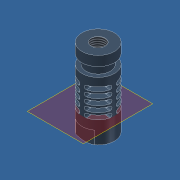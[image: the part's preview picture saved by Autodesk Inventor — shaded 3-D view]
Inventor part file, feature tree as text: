
AUTODESK INVENTOR PART (.ipt)
format: ipt  version: unknown  size: 470,016 bytes
history: native  units: mm
features: sketch x7, hole x3, extrude x3, pattern_circular x2, pattern_linear x2, revolve x1, plane x1, fillet x1, projected_geometry x1
ambient origin geometry x8: Origin, YZ Plane, XZ Plane, XY Plane, X Axis, Y Axis, Z Axis, Center Point
feature tree (21):
  revolve  "Revolution1"  [1 undecoded]
  hole  "Hole1"  [1 undecoded]
  hole  "Hole2"  [1 undecoded]
  plane  "Work Plane1"
  extrude  "Extrusion1"  Depth=4.8mm
  fillet  "Fillet2"  [1 undecoded]
  pattern_circular  "Circular Pattern1"  [2 undecoded]
  pattern_linear  "Rectangular Pattern1"  Spacing1=1.368338mm  [1 undecoded]
  extrude  "Extrusion2"  Depth=12.971287mm
  extrude  "Extrusion3"  Depth=2.0mm TaperAngle=0.0deg
  pattern_linear  "Rectangular Pattern2"  Spacing1=1.0mm  [1 undecoded]
  pattern_circular  "Circular Pattern2"  Count=4 Angle=360.0deg
  hole  "Hole4"  [1 undecoded]
  sketch  "Sketch2"  dims[d0=3.25mm d1=6.0mm]
  sketch  "Sketch3"  dims[d2=40.0mm d3=4.6mm]
  sketch  "Sketch4"  dims[d4=8.0mm d5=60.0deg]
  sketch  "Sketch5"  dims[d6=5.0mm d7=4.8mm d8=90.0deg]
  sketch  "Sketch6"  dims[d9=6.917mm d10=11.5mm d11=4.0mm d12=2.0mm d13=90.0deg d14=11.5mm d15=20.594885mm]
  sketch  "Sketch8"  dims[d16=6.917mm d17=7.6mm d18=4.0mm d19=2.0mm d20=90.0deg d21=7.5mm d22=20.594885mm]
  sketch  "Sketch9"  dims[d23=-12.5mm d24=3.8mm d26=1.368338mm d27=12.971287mm d28=2.0mm d29=0.0mm d31=1.0mm d33=40.0mm d34=360.0deg d36=50.0mm d38=3.0mm d39=8.0mm d40=13.0mm d41=6.5mm d42=8.0mm d43=2.0mm d44=0.0mm d55=2.0mm d56=2.8mm d57=2.0mm d58=0.0mm d59=40.0mm d61=3.0mm d62=40.0mm d63=360.0deg d65=8.0mm d66=6.0mm d67=4.0mm d68=2.0mm d69=90.0deg d70=3.2mm d71=20.594885mm]
  projected_geometry  "Project Cut Edges1"
note: 9 required parameter values undecoded (feature->parameter linkage not recoverable at this tier; creation-order binding heuristic only, values carry confidence <= 0.55)